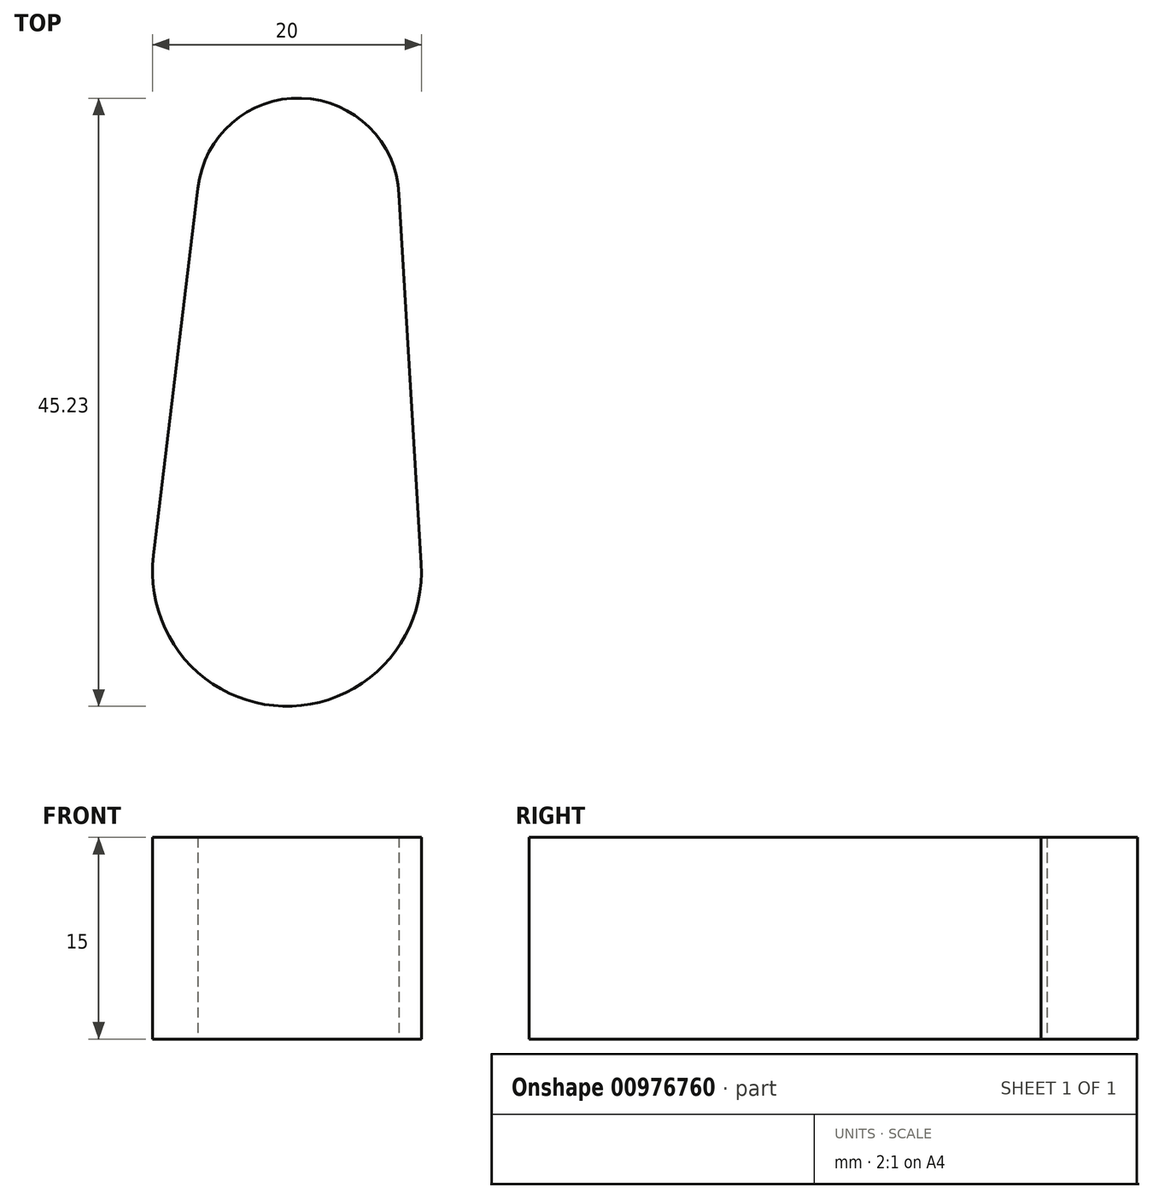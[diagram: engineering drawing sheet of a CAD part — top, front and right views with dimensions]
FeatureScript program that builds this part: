
annotation { "Feature Type Name" : "Feature", "Feature Type Description" : "" }
export const myFeature = defineFeature(function(context is Context, id is Id, definition is map)
    precondition{}
    {
        {
            var Q0;
            Q0=qCreatedBy(makeId("Top.planeOp"),FACE);
            var sketch = newSketch(context, id + "F0", { "sketchPlane" : qUnion([Q0])});
            skCircle(sketch, "E0", {"center": v(-24.42, 34.46) * mm, "radius": 7.5 * mm});
            skCircle(sketch, "E1", {"center": v(-25.26, 6.73) * mm, "radius": 10 * mm});
            skLineSegment(sketch, "E2", {"start": v(-31.88, 35.26) * mm, "end": v(-35.2, 7.94) * mm});
            skLineSegment(sketch, "E3", {"start": v(-24.42, 34.46) * mm, "end": v(-25.26, 6.73) * mm});
            skLineSegment(sketch, "E4", {"start": v(-24.42, 34.46) * mm, "end": v(-25.88, -13.44) * mm});
            skLineSegment(sketch, "E5", {"start": v(-25.88, -13.44) * mm, "end": v(-24.03, 47.28) * mm});
            skLineSegment(sketch, "E6.MirrorCS", {"start": v(-16.93, 34.8) * mm, "end": v(-15.28, 7.33) * mm});
            skSolve(sketch);
        }
        {
            var Q0;
            Q0 = qSketchRegion(id + "F0", true);
            var Q1;
            {var subQ0=sQuery(id+"F0.wireOp",EDGE,"E5");var subQ1=sQuery(id+"F0.wireOp",EDGE,"E1");var subQ2=makeQuery(id+"F0.imprint","INTERSECT",VERTEX,{"disambiguationData":[OD(1.0)],"derivedFrom":[subQ1,subQ0]});Q1=makeQuery(id+"F0.imprint","IMPRINT",FACE,{"disambiguationData":[TD([[makeQuery(id+"F0.imprint","IMPRINT",EDGE,{"disambiguationData":[TD([[subQ2,-1.0]])],"derivedFrom":subQ1}),-1.0]])]});}
            var Q2;
            {var subQ0=sQuery(id+"F0.wireOp",EDGE,"E5");var subQ1=sQuery(id+"F0.wireOp",EDGE,"E1");var subQ2=makeQuery(id+"F0.imprint","INTERSECT",VERTEX,{"disambiguationData":[OD(1.0)],"derivedFrom":[subQ1,subQ0]});Q2=makeQuery(id+"F0.imprint","IMPRINT",FACE,{"disambiguationData":[TD([[makeQuery(id+"F0.imprint","IMPRINT",EDGE,{"disambiguationData":[TD([[subQ2,1.0]])],"derivedFrom":subQ1}),-1.0]])]});}
            extrude(context, id + "F1", {"entities" : qUnion([Q0, Q1, Q2]), "depth" : 15 * mm, "offsetDistance" : 25 * mm});
        }
    });
